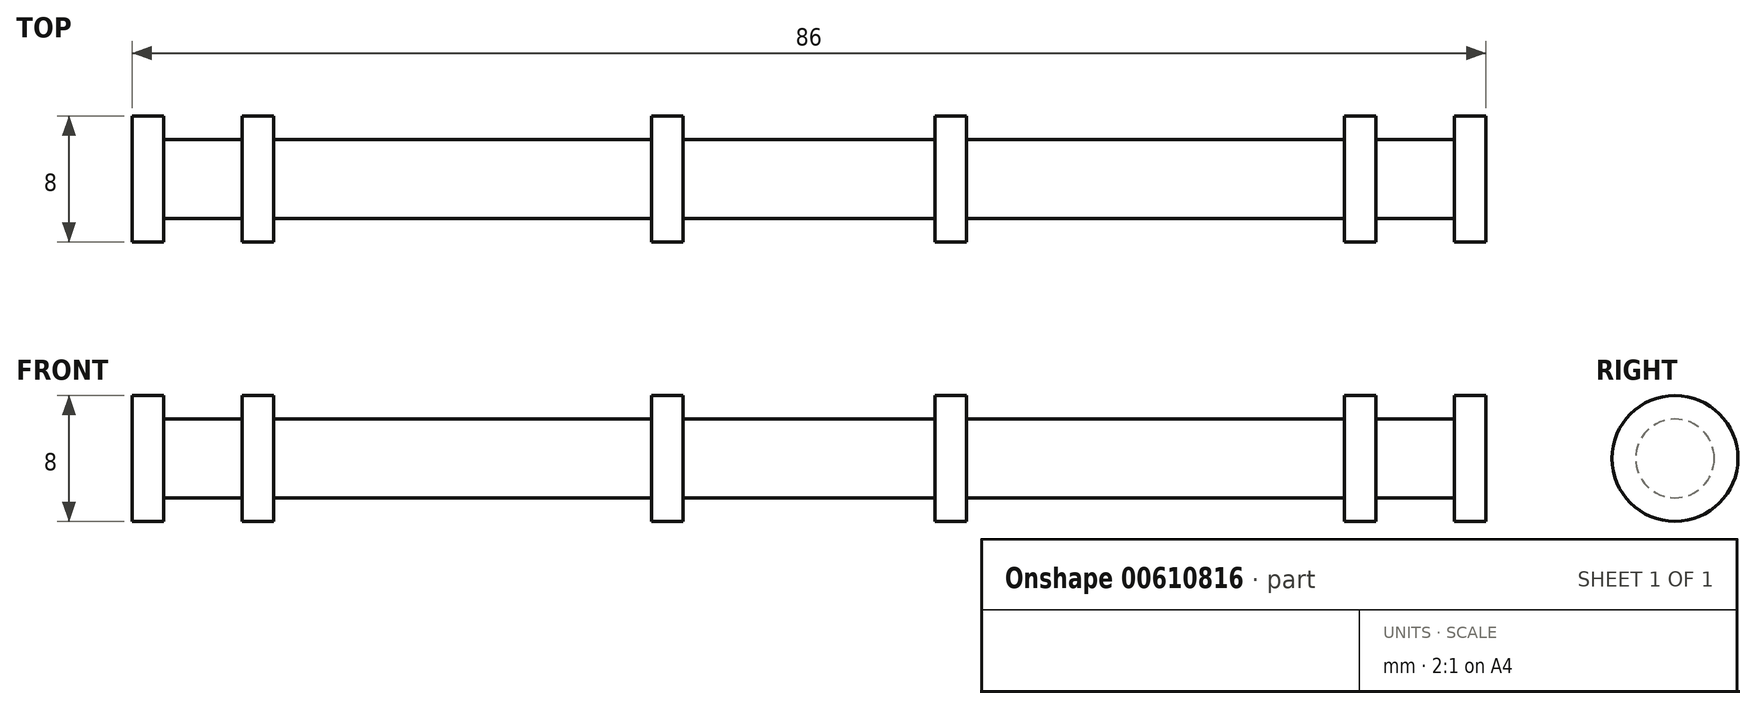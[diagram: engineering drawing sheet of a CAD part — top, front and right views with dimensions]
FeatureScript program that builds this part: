
annotation { "Feature Type Name" : "Feature", "Feature Type Description" : "" }
export const myFeature = defineFeature(function(context is Context, id is Id, definition is map)
    precondition{}
    {
        {
            var Q0;
            Q0=qCreatedBy(makeId("Right.planeOp"),FACE);
            var sketch = newSketch(context, id + "F0", { "sketchPlane" : qUnion([Q0])});
            skCircle(sketch, "E0", {"center": v(0, 0) * mm, "radius": 4 * mm});
            skSolve(sketch);
        }
        {
            var Q0;
            Q0=makeQuery(id+"F0.imprint","IMPRINT",FACE,{"disambiguationData":[TD([[makeQuery(id+"F0.imprint","IMPRINT",EDGE,{"derivedFrom":sQuery(id+"F0.wireOp",EDGE,"E0")}),1.0]])]});
            extrude(context, id + "F1", {"entities" : qUnion([Q0]), "depth" : 2 * mm, "offsetDistance" : 25 * mm});
        }
        {
            var Q0;
            Q0=makeQuery(id+"F1.opExtrude","CAP_FACE",FACE,{"disambiguationData":[OSD([sQuery(id+"F0.wireOp",EDGE,"E0")])],"isStart":false});
            var sketch = newSketch(context, id + "F2", { "sketchPlane" : qUnion([Q0])});
            skCircle(sketch, "E1", {"center": v(0, 0) * mm, "radius": 2.5 * mm});
            skSolve(sketch);
        }
        {
            var Q0;
            Q0 = qSketchRegion(id + "F2", true);
            extrude(context, id + "F3", {"entities" : qUnion([Q0]), "operationType" : NewBodyOperationType.ADD, "depth" : 5 * mm, "offsetDistance" : 25 * mm});
        }
        {
            var Q0;
            Q0=makeQuery(id+"F3.opExtrude","CAP_FACE",FACE,{"disambiguationData":[OSD([sQuery(id+"F2.wireOp",EDGE,"E1")])],"isStart":false});
            var sketch = newSketch(context, id + "F4", { "sketchPlane" : qUnion([Q0])});
            skCircle(sketch, "E2", {"center": v(0, 0) * mm, "radius": 4 * mm});
            skSolve(sketch);
        }
        {
            var Q0;
            Q0 = qSketchRegion(id + "F4", true);
            extrude(context, id + "F5", {"entities" : qUnion([Q0]), "operationType" : NewBodyOperationType.ADD, "depth" : 2 * mm, "offsetDistance" : 25 * mm});
        }
        {
            var Q0;
            Q0=makeQuery(id+"F5.opExtrude","CAP_FACE",FACE,{"disambiguationData":[OSD([sQuery(id+"F4.wireOp",EDGE,"E2")])],"isStart":false});
            var sketch = newSketch(context, id + "F6", { "sketchPlane" : qUnion([Q0])});
            skCircle(sketch, "E3", {"center": v(0, 0) * mm, "radius": 2.5 * mm});
            skSolve(sketch);
        }
        {
            var Q0;
            Q0 = qSketchRegion(id + "F6", true);
            extrude(context, id + "F7", {"entities" : qUnion([Q0]), "operationType" : NewBodyOperationType.ADD, "depth" : 24 * mm, "offsetDistance" : 25 * mm});
        }
        {
            var Q0;
            Q0=makeQuery(id+"F7.opExtrude","CAP_FACE",FACE,{"disambiguationData":[OSD([sQuery(id+"F6.wireOp",EDGE,"E3")])],"isStart":false});
            var sketch = newSketch(context, id + "F8", { "sketchPlane" : qUnion([Q0])});
            skCircle(sketch, "E4", {"center": v(0, 0) * mm, "radius": 4 * mm});
            skSolve(sketch);
        }
        {
            var Q0;
            Q0 = qSketchRegion(id + "F8", true);
            extrude(context, id + "F9", {"entities" : qUnion([Q0]), "operationType" : NewBodyOperationType.ADD, "depth" : 2 * mm, "offsetDistance" : 25 * mm});
        }
        {
            var Q0;
            Q0=makeQuery(id+"F9.opExtrude","CAP_FACE",FACE,{"disambiguationData":[OSD([sQuery(id+"F8.wireOp",EDGE,"E4")])],"isStart":false});
            var sketch = newSketch(context, id + "F10", { "sketchPlane" : qUnion([Q0])});
            skCircle(sketch, "E5", {"center": v(0, 0) * mm, "radius": 2.5 * mm});
            skSolve(sketch);
        }
        {
            var Q0;
            Q0 = qSketchRegion(id + "F10", true);
            extrude(context, id + "F11", {"entities" : qUnion([Q0]), "operationType" : NewBodyOperationType.ADD, "depth" : 16 * mm, "offsetDistance" : 25 * mm});
        }
        {
            var Q0;
            Q0=makeQuery(id+"F11.opExtrude","CAP_FACE",FACE,{"disambiguationData":[OSD([sQuery(id+"F10.wireOp",EDGE,"E5")])],"isStart":false});
            var sketch = newSketch(context, id + "F12", { "sketchPlane" : qUnion([Q0])});
            skCircle(sketch, "E6", {"center": v(0, 0) * mm, "radius": 4 * mm});
            skSolve(sketch);
        }
        {
            var Q0;
            Q0 = qSketchRegion(id + "F12", true);
            extrude(context, id + "F13", {"entities" : qUnion([Q0]), "operationType" : NewBodyOperationType.ADD, "depth" : 2 * mm, "offsetDistance" : 25 * mm});
        }
        {
            var Q0;
            Q0=makeQuery(id+"F13.opExtrude","CAP_FACE",FACE,{"disambiguationData":[OSD([sQuery(id+"F12.wireOp",EDGE,"E6")])],"isStart":false});
            var sketch = newSketch(context, id + "F14", { "sketchPlane" : qUnion([Q0])});
            skCircle(sketch, "E7", {"center": v(0, 0) * mm, "radius": 2.5 * mm});
            skSolve(sketch);
        }
        {
            var Q0;
            Q0 = qSketchRegion(id + "F14", true);
            extrude(context, id + "F15", {"entities" : qUnion([Q0]), "operationType" : NewBodyOperationType.ADD, "depth" : 24 * mm, "offsetDistance" : 25 * mm});
        }
        {
            var Q0;
            Q0=makeQuery(id+"F15.opExtrude","CAP_FACE",FACE,{"disambiguationData":[OSD([sQuery(id+"F14.wireOp",EDGE,"E7")])],"isStart":false});
            var sketch = newSketch(context, id + "F16", { "sketchPlane" : qUnion([Q0])});
            skCircle(sketch, "E8", {"center": v(0, 0) * mm, "radius": 4 * mm});
            skSolve(sketch);
        }
        {
            var Q0;
            Q0 = qSketchRegion(id + "F16", true);
            extrude(context, id + "F17", {"entities" : qUnion([Q0]), "operationType" : NewBodyOperationType.ADD, "depth" : 2 * mm, "offsetDistance" : 25 * mm});
        }
        {
            var Q0;
            Q0=makeQuery(id+"F17.opExtrude","CAP_FACE",FACE,{"disambiguationData":[OSD([sQuery(id+"F16.wireOp",EDGE,"E8")])],"isStart":false});
            var sketch = newSketch(context, id + "F18", { "sketchPlane" : qUnion([Q0])});
            skCircle(sketch, "E9", {"center": v(0, 0) * mm, "radius": 2.5 * mm});
            skSolve(sketch);
        }
        {
            var Q0;
            Q0 = qSketchRegion(id + "F18", true);
            extrude(context, id + "F19", {"entities" : qUnion([Q0]), "operationType" : NewBodyOperationType.ADD, "depth" : 5 * mm, "offsetDistance" : 25 * mm});
        }
        {
            var Q0;
            Q0=makeQuery(id+"F19.opExtrude","CAP_FACE",FACE,{"disambiguationData":[OSD([sQuery(id+"F18.wireOp",EDGE,"E9")])],"isStart":false});
            var sketch = newSketch(context, id + "F20", { "sketchPlane" : qUnion([Q0])});
            skCircle(sketch, "E10", {"center": v(0, 0) * mm, "radius": 4 * mm});
            skSolve(sketch);
        }
        {
            var Q0;
            Q0 = qSketchRegion(id + "F20", true);
            extrude(context, id + "F21", {"entities" : qUnion([Q0]), "operationType" : NewBodyOperationType.ADD, "depth" : 2 * mm, "offsetDistance" : 25 * mm});
        }
    });
